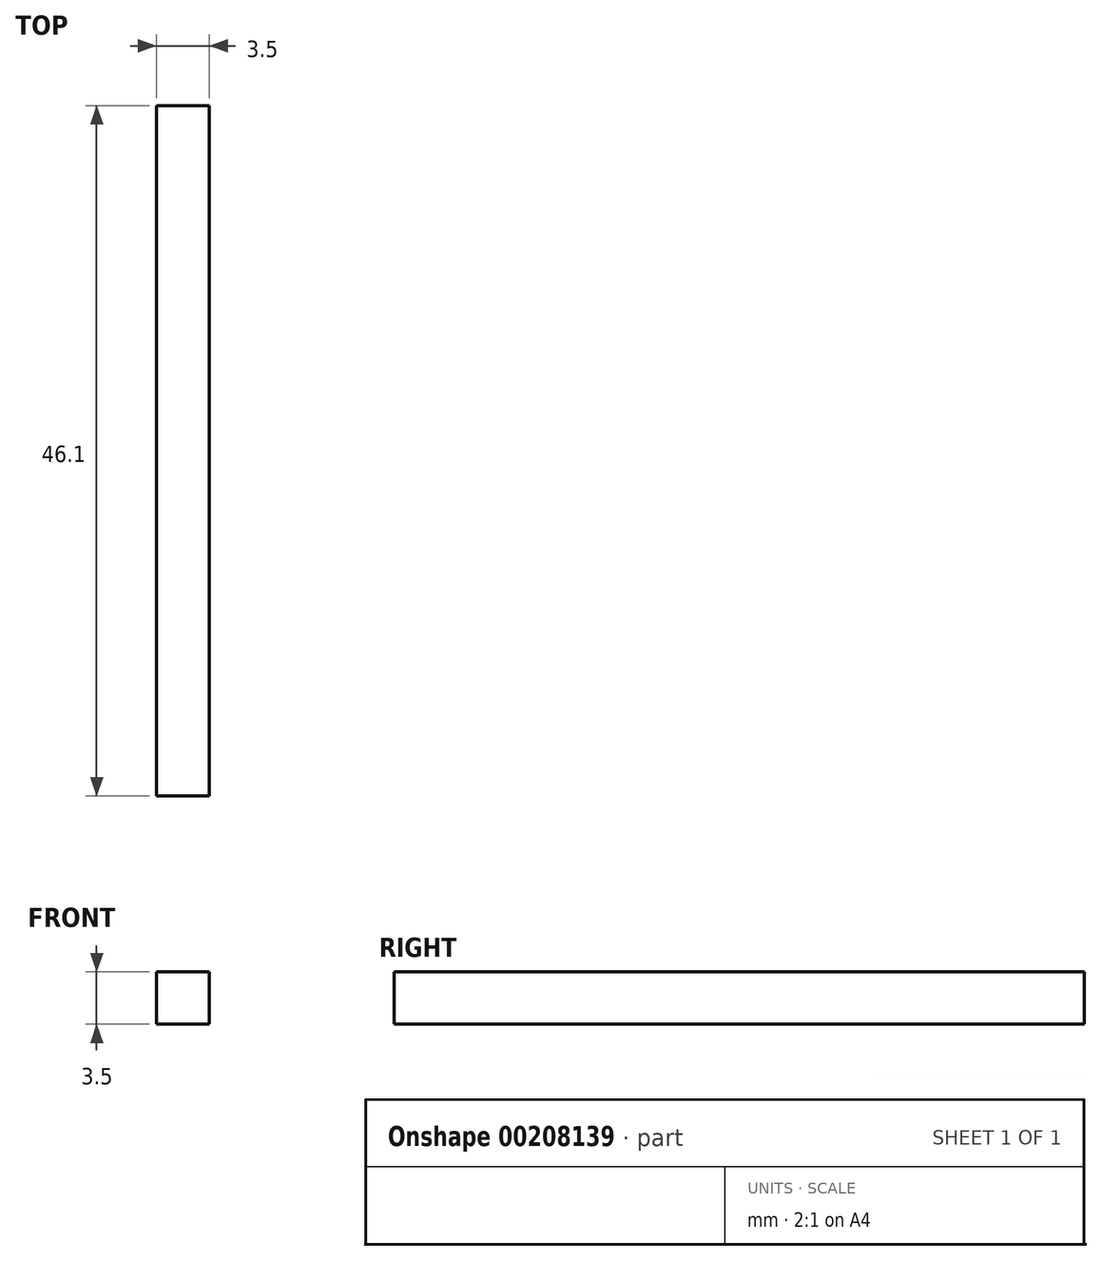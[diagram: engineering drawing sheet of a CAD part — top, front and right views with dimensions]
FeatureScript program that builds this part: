
annotation { "Feature Type Name" : "Feature", "Feature Type Description" : "" }
export const myFeature = defineFeature(function(context is Context, id is Id, definition is map)
    precondition{}
    {
        {
            var Q0;
            Q0=qCreatedBy(makeId("Top.planeOp"),FACE);
            var sketch = newSketch(context, id + "F0", { "sketchPlane" : qUnion([Q0])});
            skLineSegment(sketch, "E0.bottom", {"start": v(1.75, -23.05) * mm, "end": v(-1.75, -23.05) * mm});
            skLineSegment(sketch, "E0.top", {"start": v(1.75, 23.05) * mm, "end": v(-1.75, 23.05) * mm});
            skLineSegment(sketch, "E0.left", {"start": v(1.75, -23.05) * mm, "end": v(1.75, 23.05) * mm});
            skLineSegment(sketch, "E0.right", {"start": v(-1.75, -23.05) * mm, "end": v(-1.75, 23.05) * mm});
            skPoint(sketch, "E0.middle", {"position": v(0, 0) * mm});
            skSolve(sketch);
        }
        {
            var Q0;
            Q0 = qSketchRegion(id + "F0", true);
            extrude(context, id + "F1", {"entities" : qUnion([Q0]), "depth" : 3.5 * mm});
        }
    });
